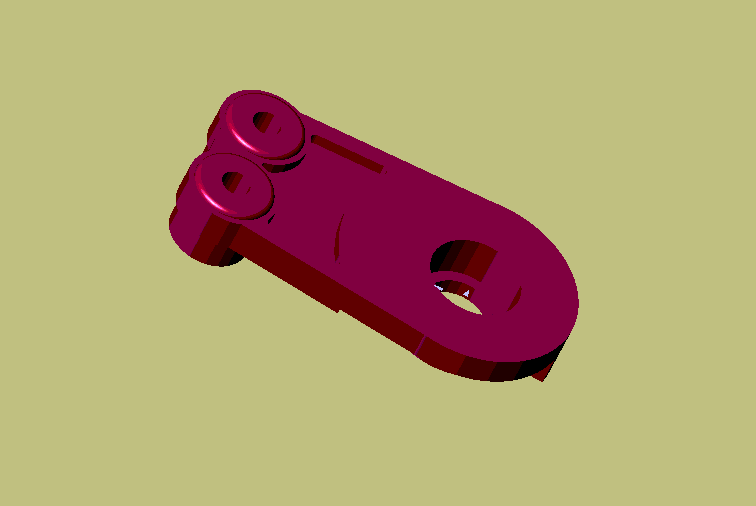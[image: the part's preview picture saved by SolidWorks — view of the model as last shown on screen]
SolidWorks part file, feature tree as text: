
SOLIDWORKS PART (.sldprt)
format: sldprt  version: not decoded by parser v0  size: 222,208 bytes
history: native  units: mm
features: sketch x10, cut_extrude x5, plane x3, fillet x3, extrude x2, material x1 (+8 scaffold rows collapsed)
feature tree (32):
  scaffold x8  (default folders/planes/origin — collapsed)
  material  "Matériau <non spécifié>"
  plane  "Plane1"
  plane  "Plane2"
  plane  "Plane3"
  sketch  "Esquisse1"  dims[c1.D2=1.5mm c1.D4=18.0mm c1.D5=8.0mm c1.D1=8.0mm c1.D3=21.0mm c2.D2=15.0mm]
  extrude  "Base-Extrusion"  Depth=3mm
  sketch  "Esquisse2"  dims[D1=7.0mm D2=7.0mm]
  extrude  "Boss.-Extru.1"  Depth=0.5mm
  fillet  "Congé1"  Radius=0.5mm
  sketch  "Esquisse3"  dims[c1.D1=24.0mm c1.D2=8.0mm c1.D3=8.0mm c2.D2=0.5mm c2.D3=0.25mm c2.D4=3.0mm]
  cut_extrude  "Enlèv. mat.-Extru.1"  Depth=1mm
  sketch  "Esquisse4"  dims[D1=2.5mm D2=2.5mm]
  sketch  "Esquisse5"  dims[D1=7.0mm D2=7.0mm]
  fillet  "Boss.-Extru.2"  Radius=3mm
  cut_extrude  "Enlèv. mat.-Extru.3"  [1 undecoded]
  sketch  "Esquisse7"
  sketch  "Esquisse9"  dims[D1=24.0mm]
  cut_extrude  "Enlèv. mat.-Extru.4"  Depth=0.5mm
  sketch  "Esquisse11"  dims[D1=12.0mm D2=3.0mm]
  fillet  "Boss.-Extru.3"  Radius=3mm
  sketch  "Esquisse12"  dims[D1=8.0mm]
  cut_extrude  "Enlèv. mat.-Extru.5"  Depth=4mm
  sketch  "Esquisse13"  dims[D1=6.0mm]
  cut_extrude  "Enlèv. mat.-Extru.6"  [1 undecoded]
decode coverage: 17 of 20 modeling features carry decoded parameters
note: 2 parameter values undecoded
note: suppression state not decoded; provenance and decode notes live in map.json
